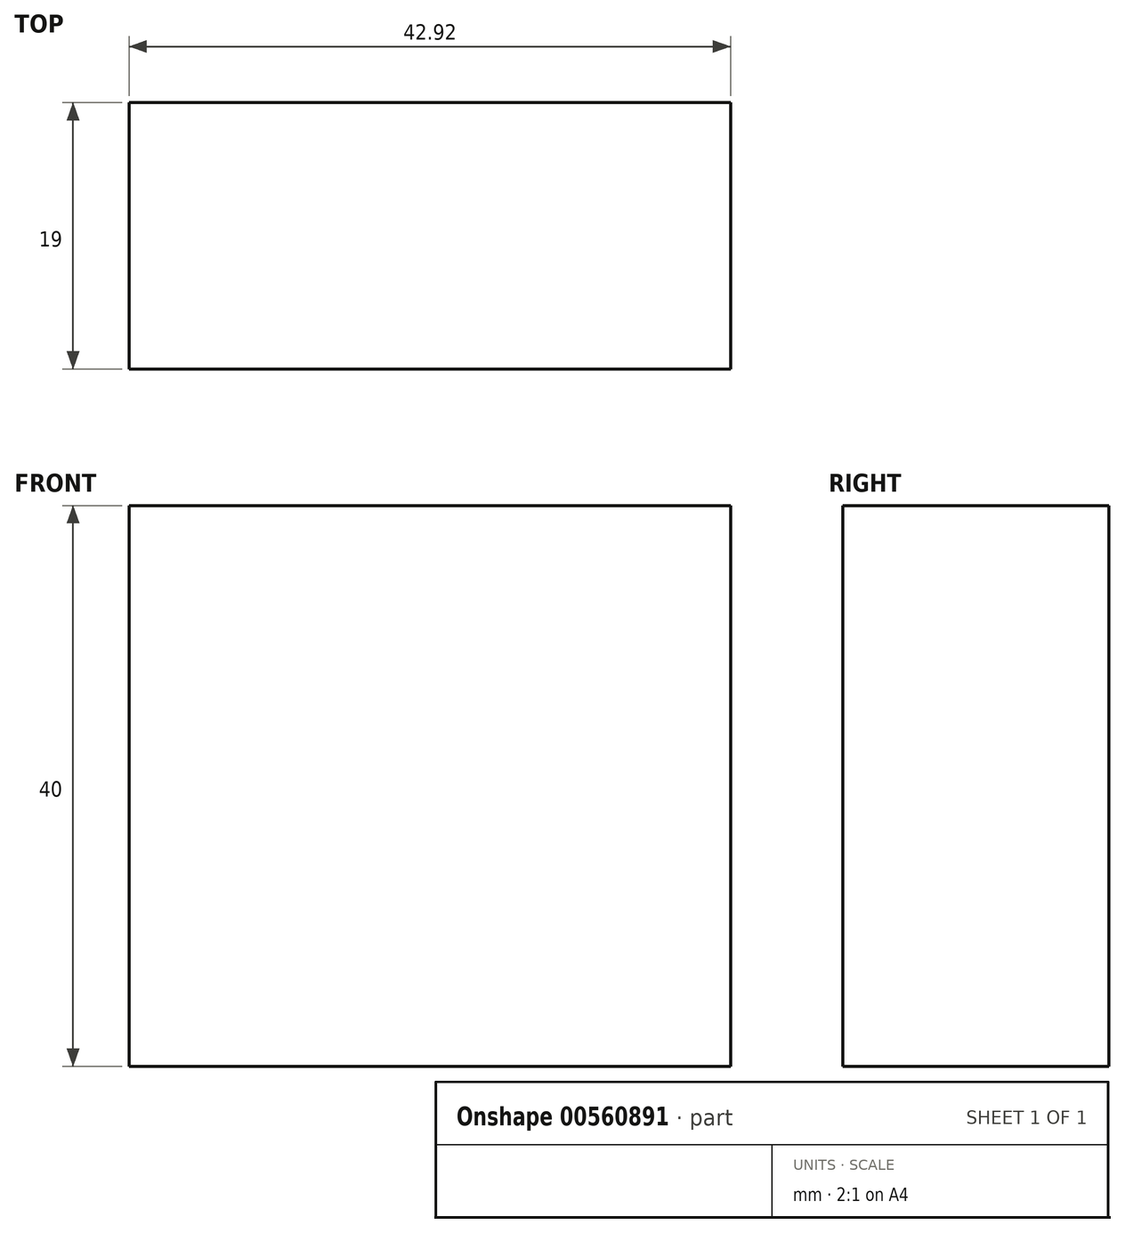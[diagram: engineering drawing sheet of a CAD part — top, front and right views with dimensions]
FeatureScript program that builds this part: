
annotation { "Feature Type Name" : "Feature", "Feature Type Description" : "" }
export const myFeature = defineFeature(function(context is Context, id is Id, definition is map)
    precondition{}
    {
        {
            var Q0;
            Q0=qCreatedBy(makeId("Front.planeOp"),FACE);
            var sketch = newSketch(context, id + "F0", { "sketchPlane" : qUnion([Q0])});
            skLineSegment(sketch, "E0.bottom", {"start": v(-21.46, 20) * mm, "end": v(21.46, 20) * mm});
            skLineSegment(sketch, "E0.top", {"start": v(-21.46, -20) * mm, "end": v(21.46, -20) * mm});
            skLineSegment(sketch, "E0.left", {"start": v(-21.46, 20) * mm, "end": v(-21.46, -20) * mm});
            skLineSegment(sketch, "E0.right", {"start": v(21.46, 20) * mm, "end": v(21.46, -20) * mm});
            skPoint(sketch, "E0.middle", {"position": v(0, 0) * mm});
            skSolve(sketch);
        }
        {
            var Q0;
            Q0=makeQuery(id+"F0.imprint","IMPRINT",FACE,{"disambiguationData":[TD([[makeQuery(id+"F0.imprint","IMPRINT",EDGE,{"derivedFrom":sQuery(id+"F0.wireOp",EDGE,"E0.bottom")}),-1.0]])]});
            extrude(context, id + "F1", {"entities" : qUnion([Q0]), "depth" : 19 * mm, "offsetDistance" : 25.4 * mm});
        }
    });
